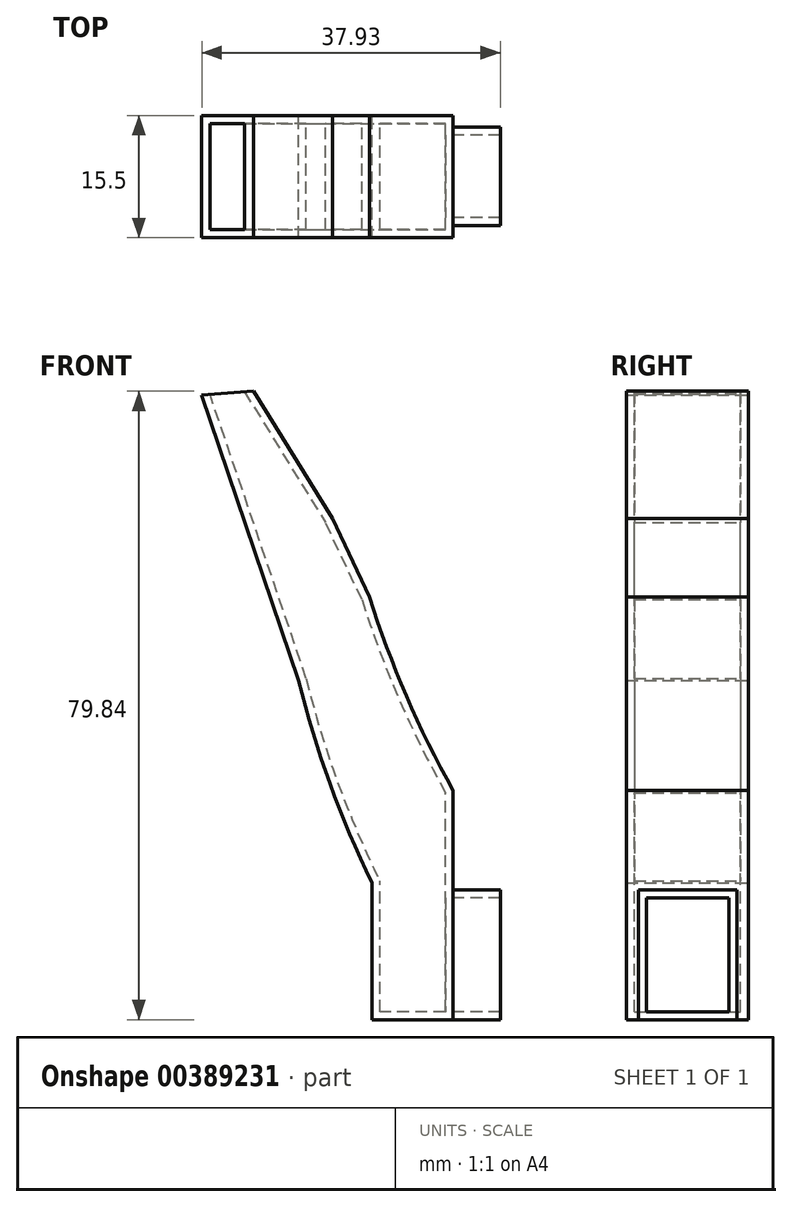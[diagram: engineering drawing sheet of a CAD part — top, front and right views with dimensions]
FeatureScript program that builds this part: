
annotation { "Feature Type Name" : "Feature", "Feature Type Description" : "" }
export const myFeature = defineFeature(function(context is Context, id is Id, definition is map)
    precondition{}
    {
        {
            var Q0;
            Q0=qCreatedBy(makeId("Front.planeOp"),FACE);
            var sketch = newSketch(context, id + "F0", { "sketchPlane" : qUnion([Q0])});
            skArc(sketch, "E0", {"start": v(-14.75, 43.15) * mm, "mid": v(-6.96, 20.7) * mm, "end": v(4.88, 0.08) * mm});
            skArc(sketch, "E1", {"start": v(-5.77, 53.8) * mm, "mid": v(-1.07, 41.22) * mm, "end": v(4.88, 29.17) * mm});
            skLineSegment(sketch, "E2", {"start": v(4.88, 0.08) * mm, "end": v(4.88, 29.17) * mm});
            skLineSegment(sketch, "E3", {"start": v(1.55, 8.35) * mm, "end": v(1.55, 8.35) * mm});
            skLineSegment(sketch, "E4", {"start": v(4.88, 0.08) * mm, "end": v(-5.44, 0.08) * mm});
            skLineSegment(sketch, "E5", {"start": v(-5.44, 0.08) * mm, "end": v(-5.44, 17.48) * mm});
            skLineSegment(sketch, "E6", {"start": v(-14.75, 43.15) * mm, "end": v(-27.05, 79.46) * mm});
            skLineSegment(sketch, "E7", {"start": v(-27.05, 79.46) * mm, "end": v(-20.5, 79.92) * mm});
            skLineSegment(sketch, "E8", {"start": v(-5.77, 53.8) * mm, "end": v(-10.47, 63.73) * mm});
            skLineSegment(sketch, "E9", {"start": v(-20.5, 79.92) * mm, "end": v(-10.47, 63.73) * mm});
            skPoint(sketch, "E10.orphan", {"position": v(-18.22, 80.08) * mm});
            skSolve(sketch);
        }
        {
            var Q0;
            Q0=makeQuery(id+"F0.imprint","IMPRINT",FACE,{"disambiguationData":[TD([[makeQuery(id+"F0.imprint","IMPRINT",EDGE,{"derivedFrom":sQuery(id+"F0.wireOp",EDGE,"E0")}),1.0]])]});
            var Q1;
            {var subQ0=sQuery(id+"F0.wireOp",EDGE,"wa6D4lD3-FdhI-6M75-mku2-y8RIMNngGbzp");Q1=makeQuery(id+"F0.imprint","IMPRINT",FACE,{"disambiguationData":[TD([[makeQuery(id+"F0.imprint","IMPRINT",EDGE,{"derivedFrom":subQ0}),-1.0]])]});}
            var Q2;
            {var subQ0=sQuery(id+"F0.wireOp",EDGE,"E4");Q2=makeQuery(id+"F0.imprint","IMPRINT",FACE,{"disambiguationData":[TD([[makeQuery(id+"F0.imprint","IMPRINT",EDGE,{"derivedFrom":subQ0}),-1.0]])]});}
            extrude(context, id + "F1", {"entities" : qUnion([Q0, Q1, Q2]), "depth" : 15.5 * mm});
        }
        {
            var Q0;
            Q0=makeQuery(id+"F1.opExtrude","SWEPT_FACE",FACE,{"disambiguationData":[OSD([sQuery(id+"F0.wireOp",EDGE,"E2")])]});
            var sketch = newSketch(context, id + "F2", { "sketchPlane" : qUnion([Q0])});
            skLineSegment(sketch, "E11.bottom", {"start": v(-1.45, 16.58) * mm, "end": v(-1.45, 0.08) * mm});
            skLineSegment(sketch, "E11.top", {"start": v(-13.95, 16.58) * mm, "end": v(-13.95, 0.08) * mm});
            skLineSegment(sketch, "E11.left", {"start": v(-1.45, 16.58) * mm, "end": v(-13.95, 16.58) * mm});
            skLineSegment(sketch, "E11.right", {"start": v(-1.45, 0.08) * mm, "end": v(-13.95, 0.08) * mm});
            skSolve(sketch);
        }
        {
            var Q0;
            Q0=makeQuery(id+"F2.imprint","IMPRINT",FACE,{"disambiguationData":[TD([[makeQuery(id+"F2.imprint","IMPRINT",EDGE,{"derivedFrom":sQuery(id+"F2.wireOp",EDGE,"E11.bottom")}),-1.0]])]});
            extrude(context, id + "F3", {"entities" : qUnion([Q0]), "operationType" : NewBodyOperationType.ADD, "depth" : 6 * mm});
        }
        {
            var Q0;
            Q0=makeQuery(id+"F1.opExtrude","SWEPT_FACE",FACE,{"disambiguationData":[OSD([sQuery(id+"F0.wireOp",EDGE,"s2g5o9kh-Ufif-MYJE-beN5-nJzxVnLCs3ak")])]});
            var Q1;
            Q1=makeQuery(id+"F1.opExtrude","SWEPT_FACE",FACE,{"disambiguationData":[OSD([sQuery(id+"F0.wireOp",EDGE,"E7")])]});
            var Q2;
            Q2=makeQuery(id+"F3.opExtrude","CAP_FACE",FACE,{"disambiguationData":[OSD([sQuery(id+"F2.wireOp",EDGE,"E11.bottom"),sQuery(id+"F2.wireOp",EDGE,"E11.top"),sQuery(id+"F2.wireOp",EDGE,"E11.left"),sQuery(id+"F2.wireOp",EDGE,"E11.right")])],"isStart":false});
            shell(context, id + "F4", {"entities" : qUnion([Q0, Q1, Q2]), "thickness" : 1 * mm});
        }
    });
